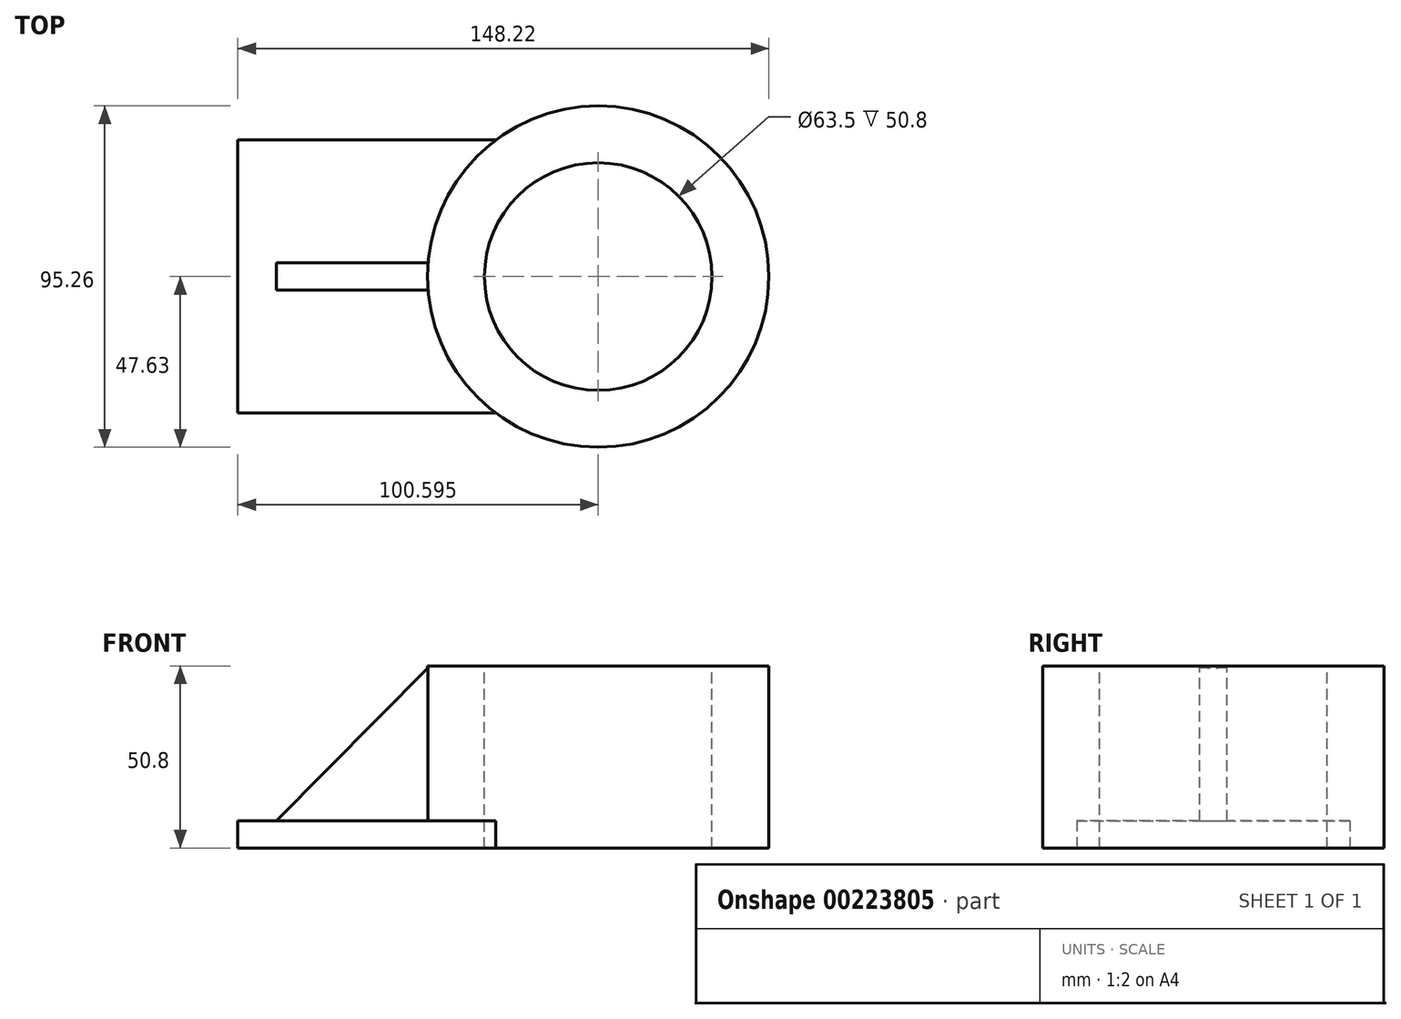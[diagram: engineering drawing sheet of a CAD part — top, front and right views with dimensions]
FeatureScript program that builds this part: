
annotation { "Feature Type Name" : "Feature", "Feature Type Description" : "" }
export const myFeature = defineFeature(function(context is Context, id is Id, definition is map)
    precondition{}
    {
        {
            var Q0;
            Q0=qCreatedBy(makeId("Front.planeOp"),FACE);
            var sketch = newSketch(context, id + "F0", { "sketchPlane" : qUnion([Q0])});
            skLineSegment(sketch, "E0.bottom", {"start": v(-75.83, 7.62) * mm, "end": v(0, 7.62) * mm});
            skLineSegment(sketch, "E0.top", {"start": v(-75.83, 0) * mm, "end": v(0, 0) * mm});
            skLineSegment(sketch, "E0.left", {"start": v(-75.83, 7.62) * mm, "end": v(-75.83, 0) * mm});
            skLineSegment(sketch, "E0.right", {"start": v(0, 7.62) * mm, "end": v(0, 0) * mm});
            skSolve(sketch);
        }
        {
            var Q0;
            Q0 = qSketchRegion(id + "F0", true);
            extrude(context, id + "F1", {"entities" : qUnion([Q0]), "endBound" : BoundingType.SYMMETRIC, "depth" : 76.2 * mm});
        }
        {
            var Q0;
            Q0=qCreatedBy(makeId("Front.planeOp"),FACE);
            var sketch = newSketch(context, id + "F2", { "sketchPlane" : qUnion([Q0])});
            skLineSegment(sketch, "E1", {"start": v(-65, 7.62) * mm, "end": v(-22.22, 50.8) * mm});
            skLineSegment(sketch, "E2", {"start": v(-22.23, 50.8) * mm, "end": v(0, 50.8) * mm});
            skLineSegment(sketch, "E3", {"start": v(0, 50.8) * mm, "end": v(0, 7.62) * mm});
            skLineSegment(sketch, "E4", {"start": v(0, 7.62) * mm, "end": v(-65, 7.62) * mm});
            skLineSegment(sketch, "E5", {"start": v(0, 7.62) * mm, "end": v(-86.67, 7.62) * mm, "construction": true});
            skSolve(sketch);
        }
        {
            var Q0;
            Q0 = qSketchRegion(id + "F2", true);
            extrude(context, id + "F3", {"entities" : qUnion([Q0]), "operationType" : NewBodyOperationType.ADD, "endBound" : BoundingType.SYMMETRIC, "depth" : 7.62 * mm});
        }
        {
            var Q0;
            Q0=makeQuery(id+"F3.opExtrude","SWEPT_FACE",FACE,{"disambiguationData":[OSD([sQuery(id+"F2.wireOp",EDGE,"E2")])]});
            var sketch = newSketch(context, id + "F4", { "sketchPlane" : qUnion([Q0])});
            skLineSegment(sketch, "E6", {"start": v(-22.22, 0) * mm, "end": v(24.77, 0) * mm, "construction": true});
            skPoint(sketch, "E6.endSnap0", {"position": v(-22.22, 0) * mm});
            skCircle(sketch, "E7", {"center": v(24.77, 0) * mm, "radius": 47.63 * mm});
            skLineSegment(sketch, "E8", {"start": v(24.77, 0) * mm, "end": v(24.77, 113.76) * mm, "construction": true});
            skLineSegment(sketch, "E9", {"start": v(24.77, 113.76) * mm, "end": v(24.77, -75.9) * mm, "construction": true});
            skSolve(sketch);
        }
        {
            var Q0;
            Q0 = qSketchRegion(id + "F4", true);
            var Q1;
            Q1=makeQuery(id+"F1.opExtrude","SWEPT_BODY",BODY,{"disambiguationData":[OSD([sQuery(id+"F0.wireOp",EDGE,"E0.bottom"),sQuery(id+"F0.wireOp",EDGE,"E0.top"),sQuery(id+"F0.wireOp",EDGE,"E0.left"),sQuery(id+"F0.wireOp",EDGE,"E0.right")])]});
            extrude(context, id + "F5", {"entities" : qUnion([Q0]), "operationType" : NewBodyOperationType.ADD, "oppositeDirection" : true, "endBoundEntityBody" : qUnion([Q1]), "depth" : 50.8 * mm});
        }
        {
            var Q0;
            Q0=makeQuery(id+"F5.boolean.opBoolean","MERGE",FACE,{"derivedFrom":[makeQuery(id+"F3.opExtrude","SWEPT_FACE",FACE,{"disambiguationData":[OSD([sQuery(id+"F2.wireOp",EDGE,"E2")])]}),makeQuery(id+"F5.opExtrude","CAP_FACE",FACE,{"disambiguationData":[OSD([sQuery(id+"F4.wireOp",EDGE,"E7")])],"isStart":true})]});
            var sketch = newSketch(context, id + "F6", { "sketchPlane" : qUnion([Q0])});
            skLineSegment(sketch, "E10", {"start": v(-35.52, 0) * mm, "end": v(138.91, 0) * mm, "construction": true});
            skCircle(sketch, "E11", {"center": v(24.77, 0) * mm, "radius": 31.75 * mm});
            skSolve(sketch);
        }
        {
            var Q0;
            Q0 = qSketchRegion(id + "F6", true);
            extrude(context, id + "F7", {"entities" : qUnion([Q0]), "operationType" : NewBodyOperationType.REMOVE, "endBound" : BoundingType.THROUGH_ALL, "oppositeDirection" : true, "depth" : 25.4 * mm});
        }
    });
